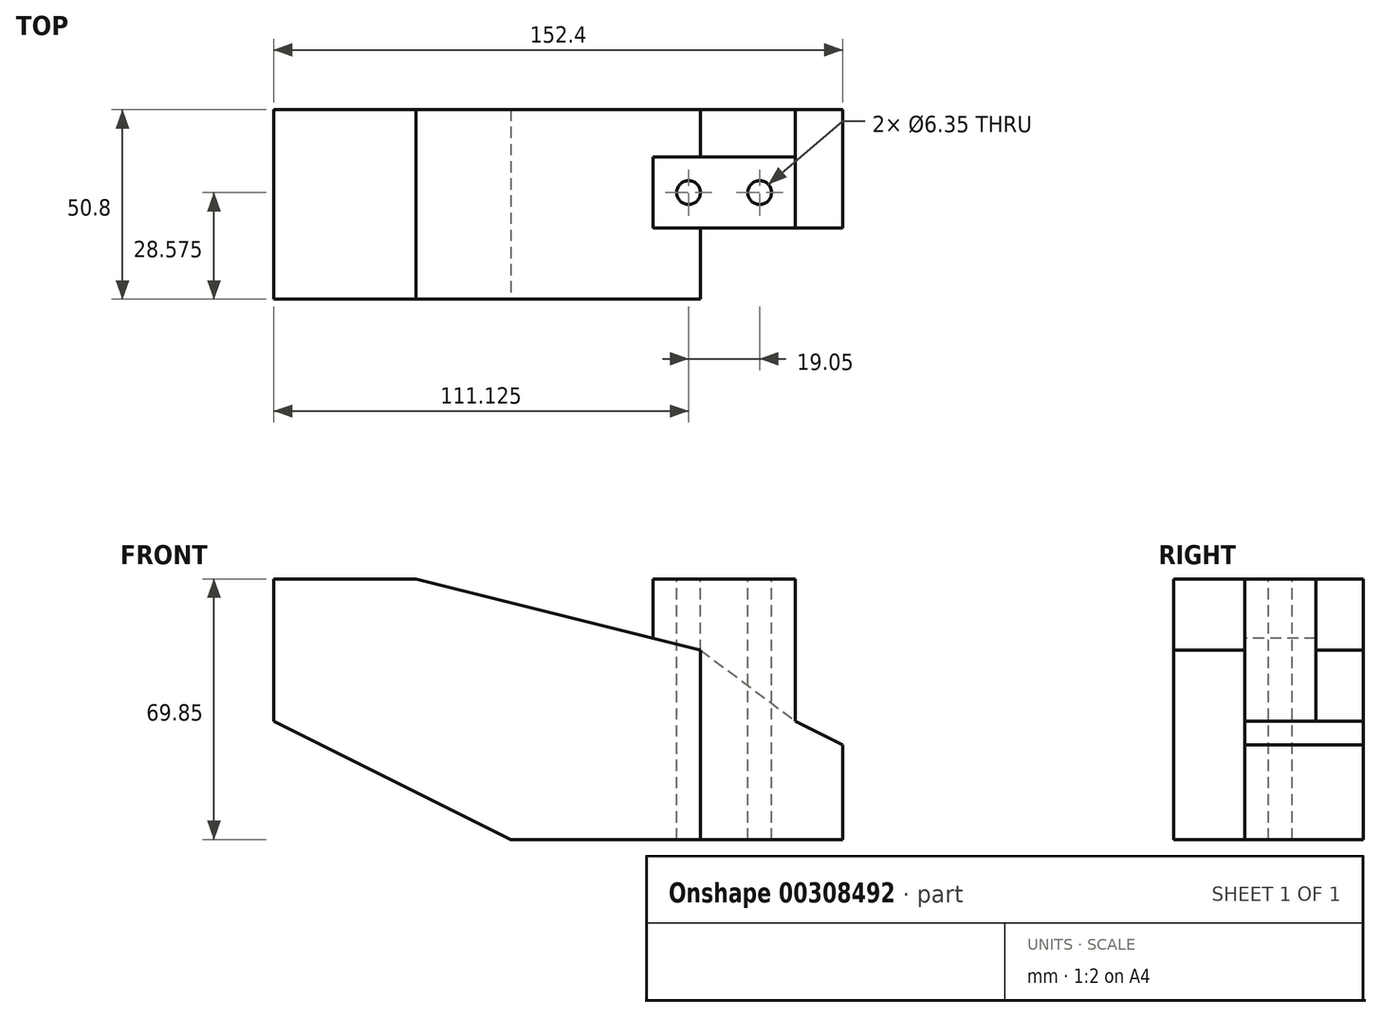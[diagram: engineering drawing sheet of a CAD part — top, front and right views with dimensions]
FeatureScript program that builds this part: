
annotation { "Feature Type Name" : "Feature", "Feature Type Description" : "" }
export const myFeature = defineFeature(function(context is Context, id is Id, definition is map)
    precondition{}
    {
        {
            var Q0;
            Q0=qCreatedBy(makeId("Front.planeOp"),FACE);
            var sketch = newSketch(context, id + "F0", { "sketchPlane" : qUnion([Q0])});
            skLineSegment(sketch, "E0.bottom", {"start": v(0, 0) * mm, "end": v(114.3, 0) * mm});
            skLineSegment(sketch, "E0.top", {"start": v(0, 69.85) * mm, "end": v(114.3, 69.85) * mm});
            skLineSegment(sketch, "E0.left", {"start": v(0, 0) * mm, "end": v(0, 69.85) * mm});
            skLineSegment(sketch, "E0.right", {"start": v(114.3, 0) * mm, "end": v(114.3, 69.85) * mm});
            skSolve(sketch);
        }
        {
            var Q0;
            Q0 = qSketchRegion(id + "F0", true);
            extrude(context, id + "F1", {"entities" : qUnion([Q0]), "oppositeDirection" : true, "depth" : 50.8 * mm});
        }
        {
            var Q0;
            Q0=makeQuery(id+"F1.opExtrude","CAP_FACE",FACE,{"disambiguationData":[OSD([sQuery(id+"F0.wireOp",EDGE,"E0.bottom"),sQuery(id+"F0.wireOp",EDGE,"E0.top"),sQuery(id+"F0.wireOp",EDGE,"E0.left"),sQuery(id+"F0.wireOp",EDGE,"E0.right")])],"isStart":true});
            var sketch = newSketch(context, id + "F2", { "sketchPlane" : qUnion([Q0])});
            skLineSegment(sketch, "E1", {"start": v(63.5, 0) * mm, "end": v(0, 31.75) * mm});
            skLineSegment(sketch, "E2", {"start": v(38.1, 69.85) * mm, "end": v(114.3, 50.8) * mm});
            skSolve(sketch);
        }
        {
            var Q0;
            {var subQ0=sQuery(id+"F2.wireOp",EDGE,"E1");Q0=makeQuery(id+"F2.imprint","IMPRINT",FACE,{"disambiguationData":[TD([[makeQuery(id+"F2.imprint","IMPRINT",EDGE,{"derivedFrom":subQ0}),1.0]])]});}
            extrude(context, id + "F3", {"entities" : qUnion([Q0]), "operationType" : NewBodyOperationType.REMOVE, "oppositeDirection" : true, "depth" : 76.2 * mm});
        }
        {
            var Q0;
            {var subQ0=sQuery(id+"F2.wireOp",EDGE,"E2");Q0=makeQuery(id+"F2.imprint","IMPRINT",FACE,{"disambiguationData":[TD([[makeQuery(id+"F2.imprint","IMPRINT",EDGE,{"derivedFrom":subQ0}),1.0]])]});}
            extrude(context, id + "F4", {"entities" : qUnion([Q0]), "operationType" : NewBodyOperationType.REMOVE, "oppositeDirection" : true, "depth" : 19.05 * mm});
        }
        {
            var Q0;
            Q0=makeQuery(id+"F1.opExtrude","CAP_FACE",FACE,{"disambiguationData":[OSD([sQuery(id+"F0.wireOp",EDGE,"E0.bottom"),sQuery(id+"F0.wireOp",EDGE,"E0.top"),sQuery(id+"F0.wireOp",EDGE,"E0.left"),sQuery(id+"F0.wireOp",EDGE,"E0.right")])],"isStart":false});
            var sketch = newSketch(context, id + "F5", { "sketchPlane" : qUnion([Q0])});
            skLineSegment(sketch, "E3", {"start": v(-38.1, 69.85) * mm, "end": v(-114.3, 50.8) * mm});
            skSolve(sketch);
        }
        {
            var Q0;
            {var subQ0=sQuery(id+"F5.wireOp",EDGE,"E3");Q0=makeQuery(id+"F5.imprint","IMPRINT",FACE,{"disambiguationData":[TD([[makeQuery(id+"F5.imprint","IMPRINT",EDGE,{"derivedFrom":subQ0}),-1.0]])]});}
            extrude(context, id + "F6", {"entities" : qUnion([Q0]), "operationType" : NewBodyOperationType.REMOVE, "oppositeDirection" : true, "depth" : 12.7 * mm});
        }
        {
            var Q0;
            Q0=makeQuery(id+"F4.boolean.opBoolean","COPY",FACE,{"derivedFrom":makeQuery(id+"F4.opExtrude","CAP_FACE",FACE,{"disambiguationData":[OSD([sQuery(id+"F0.wireOp",EDGE,"E0.top"),sQuery(id+"F0.wireOp",EDGE,"E0.right"),sQuery(id+"F2.wireOp",EDGE,"E2")])],"isStart":false})});
            var sketch = newSketch(context, id + "F7", { "sketchPlane" : qUnion([Q0])});
            skLineSegment(sketch, "E4", {"start": v(101.6, 69.85) * mm, "end": v(101.6, 53.98) * mm});
            skSolve(sketch);
        }
        {
            var Q0;
            {var subQ0=sQuery(id+"F7.wireOp",EDGE,"E4");Q0=makeQuery(id+"F7.imprint","IMPRINT",FACE,{"disambiguationData":[TD([[makeQuery(id+"F7.imprint","IMPRINT",EDGE,{"derivedFrom":subQ0}),-1.0]])]});}
            extrude(context, id + "F8", {"entities" : qUnion([Q0]), "operationType" : NewBodyOperationType.REMOVE, "oppositeDirection" : true, "depth" : 76.2 * mm});
        }
        {
            var Q0;
            Q0=makeQuery(id+"F1.opExtrude","SWEPT_FACE",FACE,{"disambiguationData":[OSD([sQuery(id+"F0.wireOp",EDGE,"E0.right")])]});
            var sketch = newSketch(context, id + "F9", { "sketchPlane" : qUnion([Q0])});
            skLineSegment(sketch, "E5.bottom", {"start": v(19.05, 69.85) * mm, "end": v(38.1, 69.85) * mm});
            skLineSegment(sketch, "E5.left", {"start": v(19.05, 69.85) * mm, "end": v(19.05, 50.8) * mm});
            skLineSegment(sketch, "E5.right", {"start": v(38.1, 69.85) * mm, "end": v(38.1, 50.8) * mm});
            skLineSegment(sketch, "E6.top", {"start": v(0, 0) * mm, "end": v(50.8, 0) * mm});
            skLineSegment(sketch, "E6.left", {"start": v(0, 50.8) * mm, "end": v(0, 0) * mm});
            skLineSegment(sketch, "E6.right", {"start": v(50.8, 50.8) * mm, "end": v(50.8, 0) * mm});
            skLineSegment(sketch, "E7", {"start": v(0, 50.8) * mm, "end": v(19.05, 50.8) * mm});
            skLineSegment(sketch, "E8", {"start": v(38.1, 50.8) * mm, "end": v(50.8, 50.8) * mm});
            skLineSegment(sketch, "E9", {"start": v(19.05, 50.8) * mm, "end": v(19.05, 0) * mm});
            skSolve(sketch);
        }
        {
            var Q0;
            Q0=makeQuery(id+"F9.imprint","IMPRINT",FACE,{"disambiguationData":[TD([[makeQuery(id+"F9.imprint","IMPRINT",EDGE,{"derivedFrom":sQuery(id+"F9.wireOp",EDGE,"E5.bottom")}),1.0]])]});
            extrude(context, id + "F10", {"entities" : qUnion([Q0]), "operationType" : NewBodyOperationType.ADD, "depth" : 38.1 * mm});
        }
        {
            var Q0;
            Q0=makeQuery(id+"F10.boolean.opBoolean","MERGE",FACE,{"derivedFrom":[makeQuery(id+"F4.boolean.opBoolean","COPY",FACE,{"derivedFrom":makeQuery(id+"F4.opExtrude","CAP_FACE",FACE,{"disambiguationData":[OSD([sQuery(id+"F0.wireOp",EDGE,"E0.top"),sQuery(id+"F0.wireOp",EDGE,"E0.right"),sQuery(id+"F2.wireOp",EDGE,"E2")])],"isStart":false})}),makeQuery(id+"F10.opExtrude","SWEPT_FACE",FACE,{"disambiguationData":[OSD([sQuery(id+"F9.wireOp",EDGE,"E5.left"),sQuery(id+"F9.wireOp",EDGE,"E9")])]})]});
            var sketch = newSketch(context, id + "F11", { "sketchPlane" : qUnion([Q0])});
            skLineSegment(sketch, "E10", {"start": v(139.7, 0) * mm, "end": v(139.7, 31.75) * mm});
            skLineSegment(sketch, "E11", {"start": v(139.7, 31.75) * mm, "end": v(152.4, 25.4) * mm});
            skLineSegment(sketch, "E12", {"start": v(139.7, 31.75) * mm, "end": v(139.7, 69.85) * mm});
            skSolve(sketch);
        }
        {
            var Q0;
            {var subQ0=sQuery(id+"F11.wireOp",EDGE,"E11");Q0=makeQuery(id+"F11.imprint","IMPRINT",FACE,{"disambiguationData":[TD([[makeQuery(id+"F11.imprint","IMPRINT",EDGE,{"derivedFrom":subQ0}),1.0]])]});}
            extrude(context, id + "F12", {"entities" : qUnion([Q0]), "operationType" : NewBodyOperationType.REMOVE, "oppositeDirection" : true, "depth" : 76.2 * mm});
        }
        {
            var Q0;
            Q0=makeQuery(id+"F10.boolean.opBoolean","MERGE",FACE,{"derivedFrom":[makeQuery(id+"F1.opExtrude","CAP_FACE",FACE,{"disambiguationData":[OSD([sQuery(id+"F0.wireOp",EDGE,"E0.bottom"),sQuery(id+"F0.wireOp",EDGE,"E0.top"),sQuery(id+"F0.wireOp",EDGE,"E0.left"),sQuery(id+"F0.wireOp",EDGE,"E0.right")])],"isStart":false}),makeQuery(id+"F10.opExtrude","SWEPT_FACE",FACE,{"disambiguationData":[OSD([sQuery(id+"F9.wireOp",EDGE,"E6.right")])]})]});
            var sketch = newSketch(context, id + "F13", { "sketchPlane" : qUnion([Q0])});
            skLineSegment(sketch, "E13", {"start": v(-114.3, 50.8) * mm, "end": v(-139.7, 31.75) * mm});
            skSolve(sketch);
        }
        {
            var Q0;
            Q0=makeQuery(id+"F13.imprint","IMPRINT",FACE,{"disambiguationData":[TD([[makeQuery(id+"F13.imprint","IMPRINT",EDGE,{"derivedFrom":sQuery(id+"F13.wireOp",EDGE,"E13")}),-1.0]])]});
            extrude(context, id + "F14", {"entities" : qUnion([Q0]), "operationType" : NewBodyOperationType.REMOVE, "oppositeDirection" : true, "depth" : 12.7 * mm});
        }
        {
            var Q0;
            {var subQ0=sQuery(id+"F0.wireOp",EDGE,"E0.right");var subQ1=sQuery(id+"F0.wireOp",EDGE,"E0.top");Q0=makeQuery(id+"F10.boolean.opBoolean","MERGE",FACE,{"derivedFrom":[makeQuery(id+"F8.boolean.opBoolean","SPLIT",FACE,{"disambiguationData":[TD([makeQuery(id+"F1.opExtrude","SWEPT_FACE",FACE,{"disambiguationData":[OSD([subQ0])]})])],"derivedFrom":makeQuery(id+"F1.opExtrude","SWEPT_FACE",FACE,{"disambiguationData":[OSD([subQ1])]})}),makeQuery(id+"F10.opExtrude","SWEPT_FACE",FACE,{"disambiguationData":[OSD([sQuery(id+"F9.wireOp",EDGE,"E5.bottom")])]})]});}
            var sketch = newSketch(context, id + "F15", { "sketchPlane" : qUnion([Q0])});
            skCircle(sketch, "E14", {"center": v(111.13, 28.58) * mm, "radius": 3.18 * mm});
            skPoint(sketch, "E14.centerSnap0", {"position": v(101.6, 28.58) * mm});
            skCircle(sketch, "E15", {"center": v(130.18, 28.58) * mm, "radius": 3.18 * mm});
            skPoint(sketch, "E15.centerSnap0", {"position": v(139.7, 28.58) * mm});
            skSolve(sketch);
        }
        {
            var Q0;
            Q0 = qSketchRegion(id + "F15", true);
            extrude(context, id + "F16", {"entities" : qUnion([Q0]), "operationType" : NewBodyOperationType.REMOVE, "oppositeDirection" : true, "depth" : 76.2 * mm});
        }
    });
